# Revit family: POR_Solea_R0098_BIM_FR
name_source: partatom
category: Plumbing Fixtures
revit_build: Autodesk Revit 2017 (Build: 20171027_0315(x64)
units: mm (PartAtom-declared; Revit-internal decimal feet)

## family parameters
Always vertical = No
Cut with Voids When Loaded = No
OmniClass Number = 23.45.00.00
OmniClass Title = Sanitary, Laundry, and Cleaning Equipment
Part Type = Normal
Room Calculation Point = No
Round Connector Dimension = Use Diameter
Shared = No
Work Plane-Based = No

## types (1)
- P0098AC - SOLEA M2 F/PLATE DUAL/FLUSH WHITE - PO
    BOSUseNativeGeometries = 1
    Brand url = http://www.idealstandard.co.uk
    Dimensions = 247 x 19 x 165 mm
    Edition number = 1
    GTIN code = https://3391500579071
    Hauteur = 165 mm
    Installation instructions = https://www.idealstandard.fr
    Largeur = 247 mm
    Longueur = 19 mm
    Manufacturer name = Ideal Standard
    Model = P0098AC
    Product Guid = b0acee2f-9ac6-4231-be09-f45a84d4837f
    Product SKU = P0098
    Product certification = https://www.idealstandard.fr
    Product data url = https://bimobject.com
    Product name = SOLEA  M2 PLATE WH DF - PO
    Product url = https://www.idealstandard.fr
    QR code = http://bimobject.com

## geometry (parser evidence)
native form markers: Sweep x3
no freeform markers — native parametric forms only
